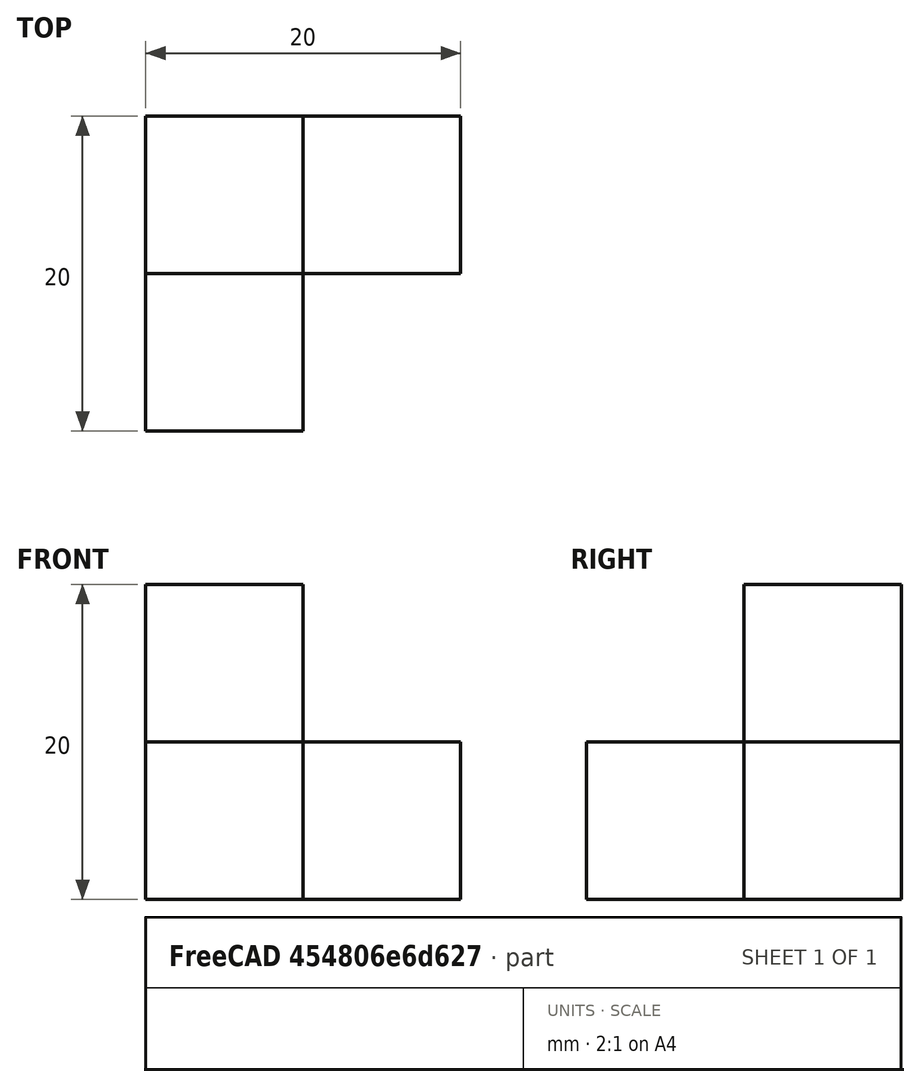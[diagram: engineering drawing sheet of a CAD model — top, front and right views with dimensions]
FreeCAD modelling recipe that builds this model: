
FCSTD DOCUMENT  (FreeCAD 0.20R29177 (Git))
Label: EjercicioVideo4
License: All rights reserved
LicenseURL: http://en.wikipedia.org/wiki/All_rights_reserved
objects: Part::Box×4, Part::MultiFuse×3
note: 7 computed .brp shape members not serialized (recipe doc carries the construction recipe); baked Part::Feature solids carry a one-line shape summary decoded from their .brp

FEATURE [Part::Box] Box  label="Nivel1-Cubo1"
  AttacherType = Attacher::AttachEngine3D
  Height = 10
  Length = 10
  Width = 10
FEATURE [Part::Box] Box001  label="Nivel2-Cubocentro"
  AttacherType = Attacher::AttachEngine3D
  Height = 10
  Length = 10
  Placement = pos=(0,0,-10) rot=(0,0,1;0rad)
  Width = 10
FEATURE [Part::Box] Box002  label="Nivel2-Cubo1"
  AttacherType = Attacher::AttachEngine3D
  Height = 10
  Length = 10
  Placement = pos=(0,-10,-10) rot=(0,0,1;0rad)
  Width = 10
FEATURE [Part::Box] Box003  label="Nivel2-Cubo2"
  AttacherType = Attacher::AttachEngine3D
  Height = 10
  Length = 10
  Placement = pos=(10,0,-10) rot=(0,0,1;0rad)
  Width = 10
FEATURE [Part::MultiFuse] Fusion
  Refine = true
  Shapes = -> [Box,Box001]
FEATURE [Part::MultiFuse] Fusion001
  Refine = true
  Shapes = -> [Box003,Box002]
FEATURE [Part::MultiFuse] Fusion002
  Refine = true
  Shapes = -> [Fusion,Fusion001]
